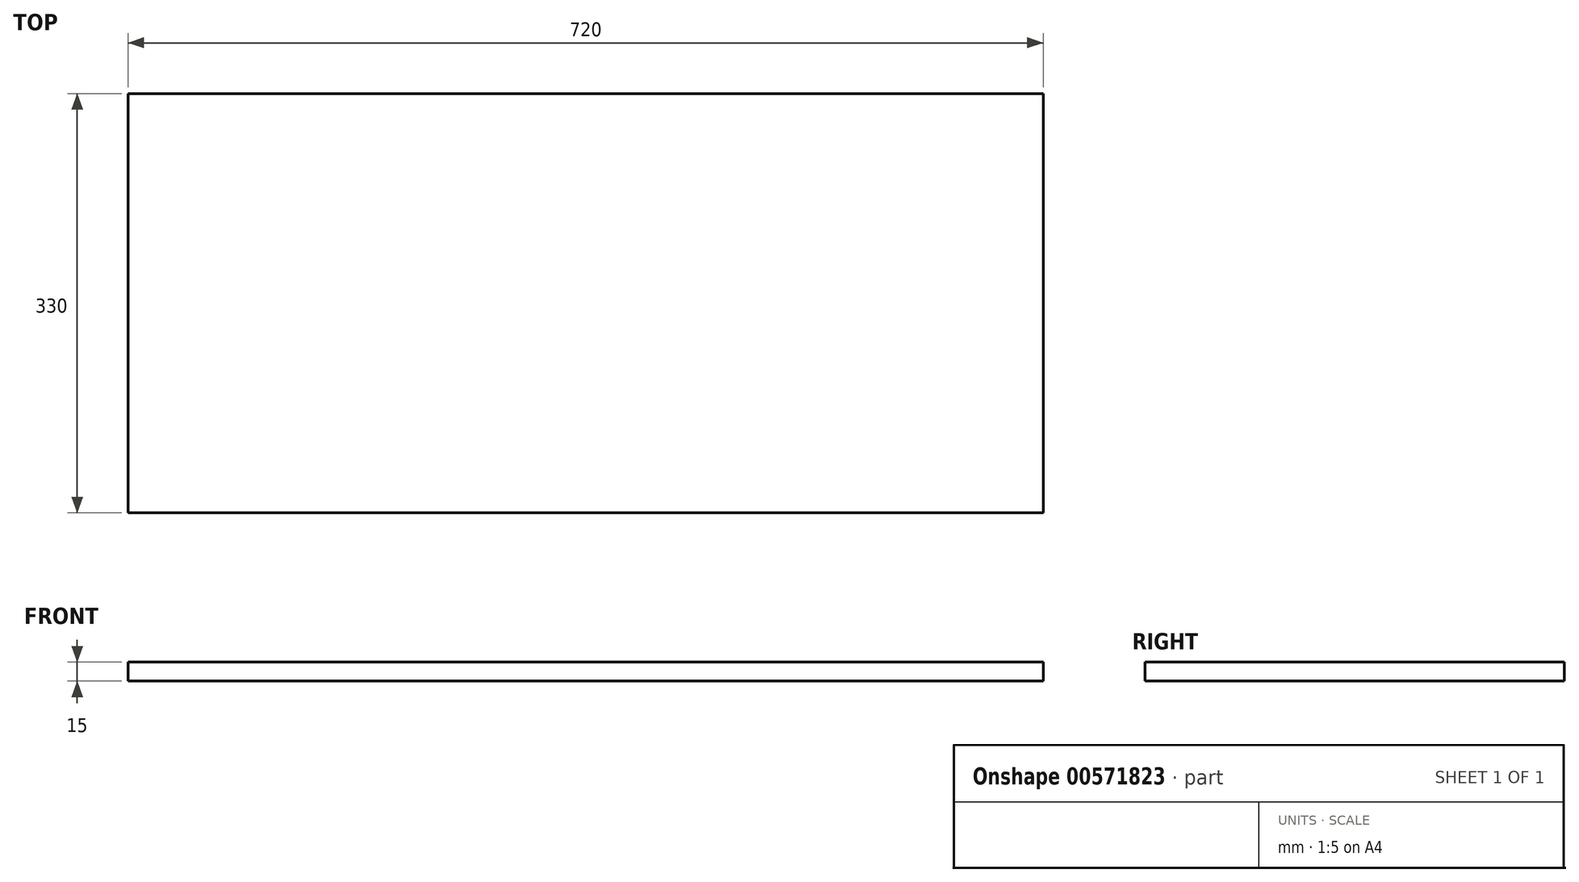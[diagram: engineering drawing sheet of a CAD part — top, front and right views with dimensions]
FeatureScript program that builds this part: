
annotation { "Feature Type Name" : "Feature", "Feature Type Description" : "" }
export const myFeature = defineFeature(function(context is Context, id is Id, definition is map)
    precondition{}
    {
        {
            var Q0;
            Q0=qCreatedBy(makeId("Front.planeOp"),FACE);
            var sketch = newSketch(context, id + "F0", { "sketchPlane" : qUnion([Q0])});
            skLineSegment(sketch, "E0.bottom", {"start": v(-49.4, 0) * mm, "end": v(670.6, 0) * mm});
            skLineSegment(sketch, "E0.top", {"start": v(-49.4, 15) * mm, "end": v(670.6, 15) * mm});
            skLineSegment(sketch, "E0.left", {"start": v(-49.4, 0) * mm, "end": v(-49.4, 15) * mm});
            skLineSegment(sketch, "E0.right", {"start": v(670.6, 0) * mm, "end": v(670.6, 15) * mm});
            skSolve(sketch);
        }
        {
            var Q0;
            Q0 = qSketchRegion(id + "F0", true);
            extrude(context, id + "F1", {"entities" : qUnion([Q0]), "oppositeDirection" : true, "depth" : 330 * mm, "offsetDistance" : 25 * mm});
        }
    });
